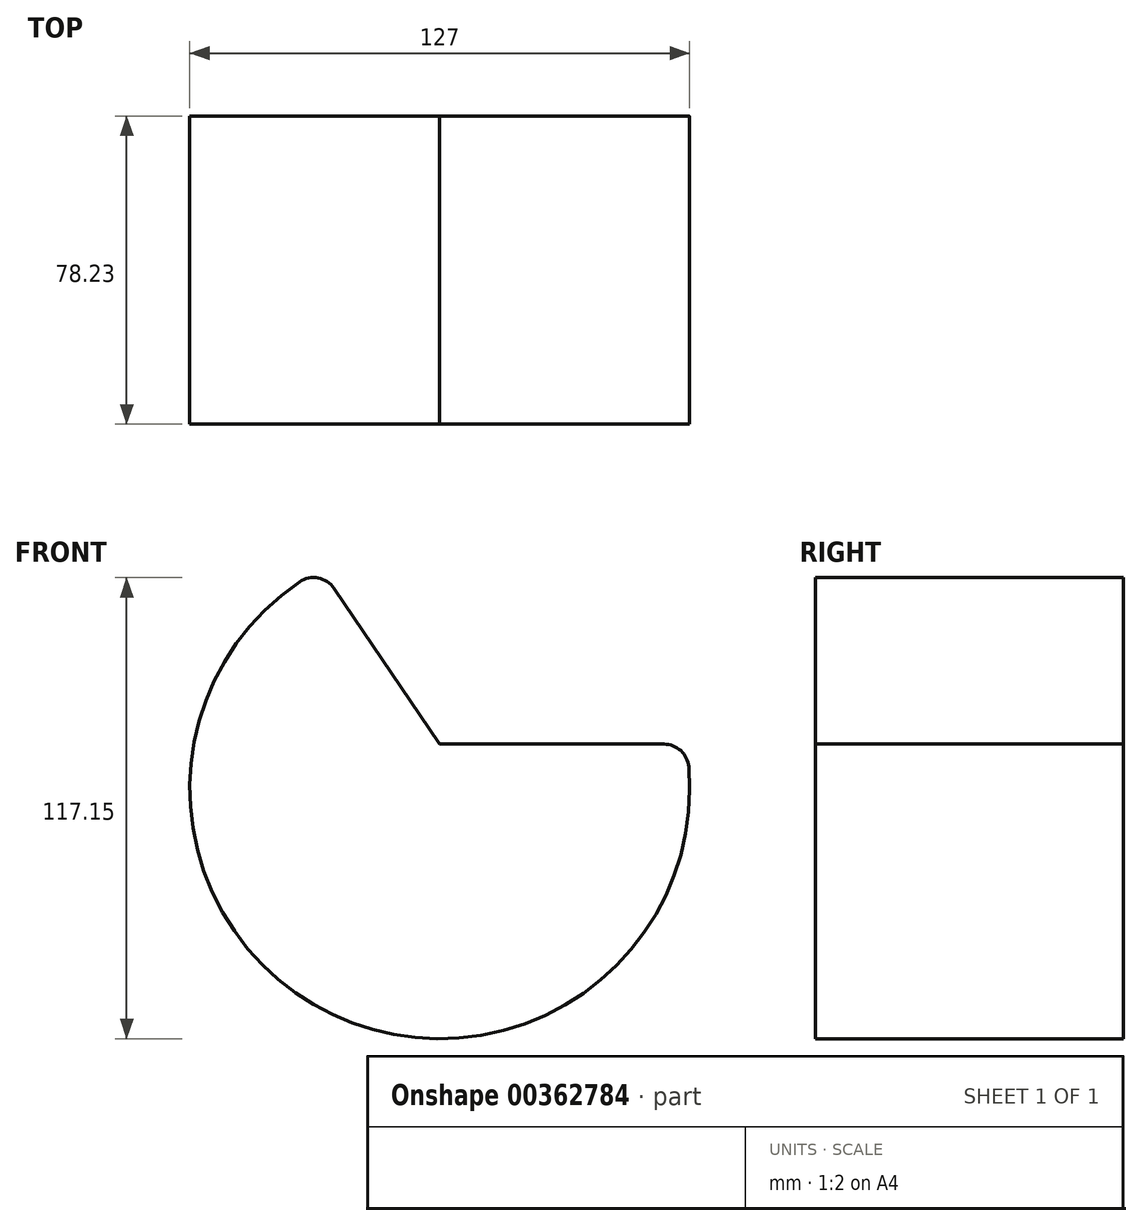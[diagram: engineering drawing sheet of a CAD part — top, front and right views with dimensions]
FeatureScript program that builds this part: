
annotation { "Feature Type Name" : "Feature", "Feature Type Description" : "" }
export const myFeature = defineFeature(function(context is Context, id is Id, definition is map)
    precondition{}
    {
        {
            var Q0;
            Q0=qCreatedBy(makeId("Front.planeOp"),FACE);
            var sketch = newSketch(context, id + "F0", { "sketchPlane" : qUnion([Q0])});
            skArc(sketch, "E0", {"start": v(-35.64, 52.55) * mm, "mid": v(-27.26, -57.35) * mm, "end": v(63.26, 5.54) * mm});
            skLineSegment(sketch, "E1", {"start": v(-26.82, 50.86) * mm, "end": v(0, 11.34) * mm});
            skLineSegment(sketch, "E2", {"start": v(0, 11.34) * mm, "end": v(56.93, 11.34) * mm});
            skPoint(sketch, "E3.visualSharp", {"position": v(-30.21, 55.85) * mm});
            skArc(sketch, "E3.filletArc", {"start": v(-26.82, 50.86) * mm, "mid": v(-30.88, 53.53) * mm, "end": v(-35.64, 52.55) * mm});
            skPoint(sketch, "E4.visualSharp", {"position": v(62.48, 11.34) * mm});
            skArc(sketch, "E4.filletArc", {"start": v(63.26, 5.54) * mm, "mid": v(61.22, 9.67) * mm, "end": v(56.93, 11.34) * mm});
            skSolve(sketch);
        }
        {
            var Q0;
            Q0=makeQuery(id+"F0.imprint","IMPRINT",FACE,{"disambiguationData":[TD([[makeQuery(id+"F0.imprint","IMPRINT",EDGE,{"derivedFrom":sQuery(id+"F0.wireOp",EDGE,"E0")}),1.0]])]});
            extrude(context, id + "F1", {"entities" : qUnion([Q0]), "depth" : 78.23 * mm});
        }
    });
